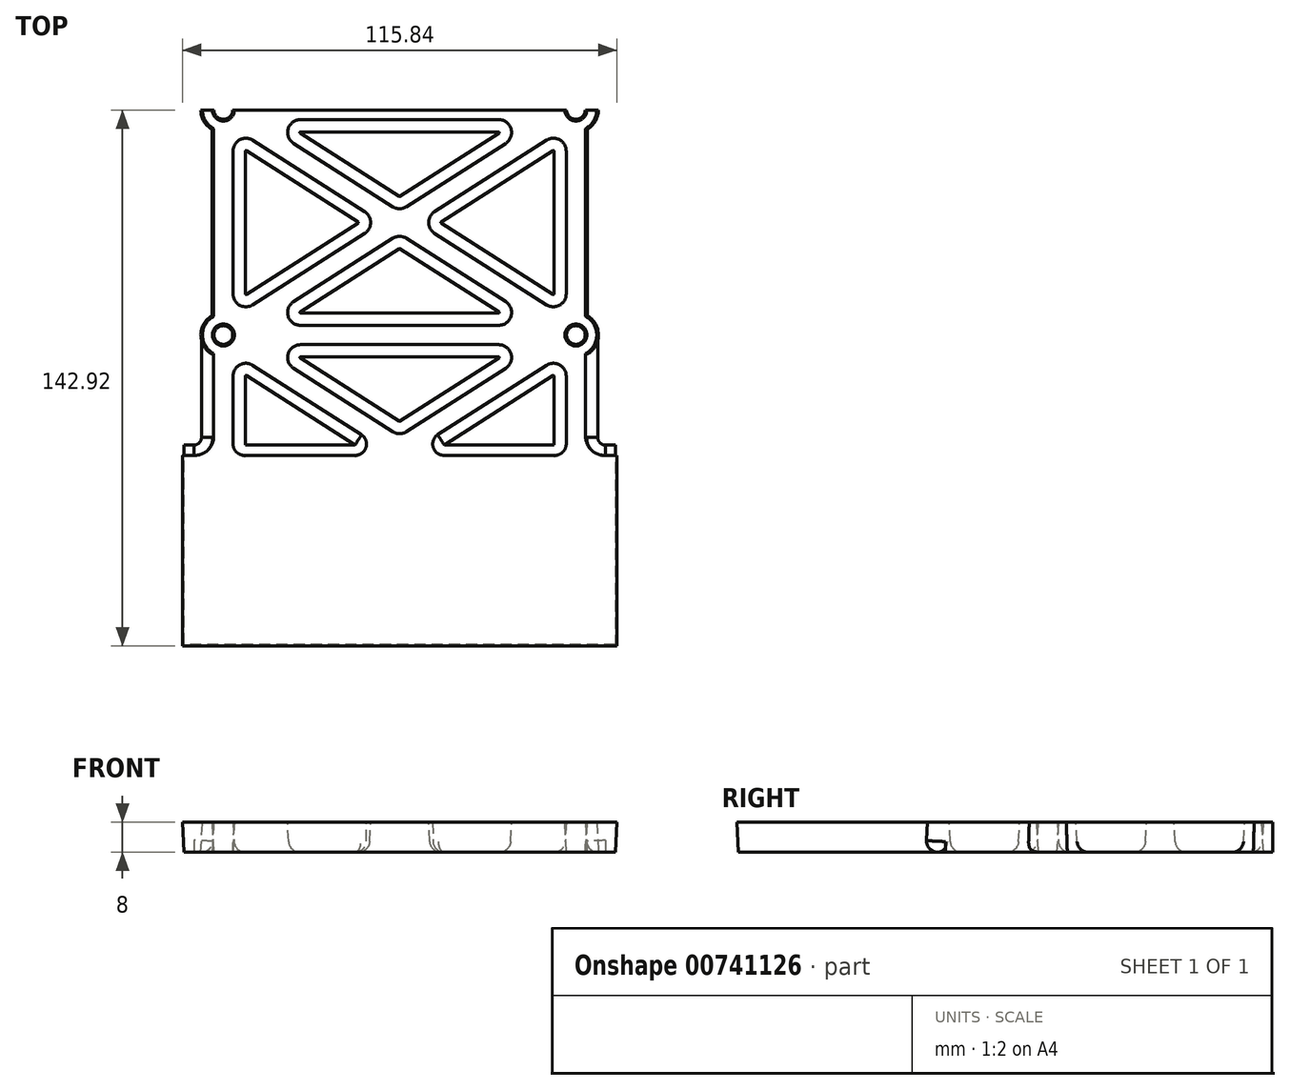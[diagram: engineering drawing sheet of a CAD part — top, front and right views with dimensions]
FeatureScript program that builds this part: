
annotation { "Feature Type Name" : "Feature", "Feature Type Description" : "" }
export const myFeature = defineFeature(function(context is Context, id is Id, definition is map)
    precondition{}
    {
        {
            var Q0;
            Q0=qCreatedBy(makeId("Top.planeOp"),FACE);
            var sketch = newSketch(context, id + "F0", { "sketchPlane" : qUnion([Q0])});
            skArc(sketch, "E0", {"start": v(49.5, 0) * mm, "mid": v(47, 2.5) * mm, "end": v(44.5, 0) * mm});
            skArc(sketch, "E1", {"start": v(53, 0) * mm, "mid": v(52.2, 3) * mm, "end": v(50, 5.2) * mm});
            skArc(sketch, "E2.0.1.0", {"start": v(50, 54.8) * mm, "mid": v(53, 60) * mm, "end": v(50, 65.2) * mm});
            skCircle(sketch, "E2.0.1.1", {"center": v(47, 60) * mm, "radius": 2.5 * mm});
            skArc(sketch, "E2.0.2.0", {"start": v(50, 114.8) * mm, "mid": v(51.24, 124.24) * mm, "end": v(41.8, 123) * mm});
            skCircle(sketch, "E2.0.2.1", {"center": v(47, 120) * mm, "radius": 2.5 * mm});
            skArc(sketch, "E2.1.0.0", {"start": v(-50, 5.2) * mm, "mid": v(-52.2, 3) * mm, "end": v(-53, 0) * mm});
            skArc(sketch, "E2.1.0.1", {"start": v(-44.5, 0) * mm, "mid": v(-47, 2.5) * mm, "end": v(-49.5, 0) * mm});
            skArc(sketch, "E2.1.1.0", {"start": v(-50, 65.2) * mm, "mid": v(-53, 60) * mm, "end": v(-50, 54.8) * mm});
            skCircle(sketch, "E2.1.1.1", {"center": v(-47, 60) * mm, "radius": 2.5 * mm});
            skArc(sketch, "E2.1.2.0", {"start": v(-41.8, 123) * mm, "mid": v(-51.24, 124.24) * mm, "end": v(-50, 114.8) * mm});
            skCircle(sketch, "E2.1.2.1", {"center": v(-47, 120) * mm, "radius": 2.5 * mm});
            skLineSegment(sketch, "E2.direction1", {"start": v(44.5, 0) * mm, "end": v(-44.5, 0) * mm, "construction": true});
            skLineSegment(sketch, "E3.0", {"start": v(-44, 109.05) * mm, "end": v(-44, 70.95) * mm});
            skLineSegment(sketch, "E3.1", {"start": v(-9.54, 92.53) * mm, "end": v(-39.39, 111.58) * mm});
            skLineSegment(sketch, "E3.2", {"start": v(-9.54, 87.47) * mm, "end": v(-39.39, 68.42) * mm});
            skArc(sketch, "E4.filletArc", {"start": v(-9.54, 87.47) * mm, "mid": v(-8.15, 90) * mm, "end": v(-9.54, 92.53) * mm});
            skArc(sketch, "E5.filletArc", {"start": v(-44, 70.95) * mm, "mid": v(-42.44, 68.32) * mm, "end": v(-39.39, 68.42) * mm});
            skArc(sketch, "E6.filletArc", {"start": v(-39.39, 111.58) * mm, "mid": v(-42.44, 111.68) * mm, "end": v(-44, 109.05) * mm});
            skLineSegment(sketch, "E7.0", {"start": v(26.45, 117) * mm, "end": v(-26.45, 117) * mm});
            skLineSegment(sketch, "E7.1", {"start": v(28.06, 111.47) * mm, "end": v(1.61, 94.59) * mm});
            skLineSegment(sketch, "E7.2", {"start": v(-1.61, 94.59) * mm, "end": v(-28.06, 111.47) * mm});
            skArc(sketch, "E8.filletArc", {"start": v(-26.45, 117) * mm, "mid": v(-29.33, 114.84) * mm, "end": v(-28.06, 111.47) * mm});
            skArc(sketch, "E9.filletArc", {"start": v(28.06, 111.47) * mm, "mid": v(29.33, 114.84) * mm, "end": v(26.45, 117) * mm});
            skArc(sketch, "E10.filletArc", {"start": v(-1.61, 94.59) * mm, "mid": v(0, 94.12) * mm, "end": v(1.61, 94.59) * mm});
            skLineSegment(sketch, "E11.0", {"start": v(-50, 114.8) * mm, "end": v(-50, 65.2) * mm});
            skLineSegment(sketch, "E12.0", {"start": v(41.8, 123) * mm, "end": v(-41.8, 123) * mm});
            skLineSegment(sketch, "E13.MirrorCS", {"start": v(44, 109.05) * mm, "end": v(44, 70.95) * mm});
            skArc(sketch, "E14.MirrorCS", {"start": v(39.39, 111.58) * mm, "mid": v(42.44, 111.68) * mm, "end": v(44, 109.05) * mm});
            skLineSegment(sketch, "E15.MirrorCS", {"start": v(9.54, 92.53) * mm, "end": v(39.39, 111.58) * mm});
            skArc(sketch, "E16.MirrorCS", {"start": v(9.54, 87.47) * mm, "mid": v(8.15, 90) * mm, "end": v(9.54, 92.53) * mm});
            skLineSegment(sketch, "E17.MirrorCS", {"start": v(9.54, 87.47) * mm, "end": v(39.39, 68.42) * mm});
            skArc(sketch, "E18.MirrorCS", {"start": v(44, 70.95) * mm, "mid": v(42.44, 68.32) * mm, "end": v(39.39, 68.42) * mm});
            skLineSegment(sketch, "E19.MirrorCS", {"start": v(26.45, 63) * mm, "end": v(-26.45, 63) * mm});
            skArc(sketch, "E20.MirrorCS", {"start": v(28.06, 68.53) * mm, "mid": v(29.33, 65.16) * mm, "end": v(26.45, 63) * mm});
            skLineSegment(sketch, "E21.MirrorCS", {"start": v(28.06, 68.53) * mm, "end": v(1.61, 85.41) * mm});
            skLineSegment(sketch, "E22.MirrorCS", {"start": v(-1.61, 85.41) * mm, "end": v(-28.06, 68.53) * mm});
            skArc(sketch, "E23.MirrorCS", {"start": v(-26.45, 63) * mm, "mid": v(-29.33, 65.16) * mm, "end": v(-28.06, 68.53) * mm});
            skArc(sketch, "E24.MirrorCS", {"start": v(-1.61, 85.41) * mm, "mid": v(0, 85.88) * mm, "end": v(1.61, 85.41) * mm});
            skLineSegment(sketch, "E25.0", {"start": v(50, 114.8) * mm, "end": v(50, 65.2) * mm});
            skArc(sketch, "E26.MirrorCS", {"start": v(-1.61, 34.59) * mm, "mid": v(0, 34.12) * mm, "end": v(1.61, 34.59) * mm});
            skArc(sketch, "E27.MirrorCS", {"start": v(-1.61, 25.41) * mm, "mid": v(0, 25.88) * mm, "end": v(1.61, 25.41) * mm});
            skArc(sketch, "E28.MirrorCS", {"start": v(39.39, 8.42) * mm, "mid": v(42.44, 8.32) * mm, "end": v(44, 10.95) * mm});
            skArc(sketch, "E29.MirrorCS", {"start": v(-26.45, 57) * mm, "mid": v(-29.33, 54.84) * mm, "end": v(-28.06, 51.47) * mm});
            skArc(sketch, "E30.MirrorCS", {"start": v(44, 49.05) * mm, "mid": v(42.44, 51.68) * mm, "end": v(39.39, 51.58) * mm});
            skArc(sketch, "E31.MirrorCS", {"start": v(9.54, 32.53) * mm, "mid": v(8.15, 30) * mm, "end": v(9.54, 27.47) * mm});
            skArc(sketch, "E32.MirrorCS", {"start": v(28.06, 51.47) * mm, "mid": v(29.33, 54.84) * mm, "end": v(26.45, 57) * mm});
            skArc(sketch, "E33.MirrorCS", {"start": v(-39.39, 8.42) * mm, "mid": v(-42.44, 8.32) * mm, "end": v(-44, 10.95) * mm});
            skArc(sketch, "E34.MirrorCS", {"start": v(-44, 49.05) * mm, "mid": v(-42.44, 51.68) * mm, "end": v(-39.39, 51.58) * mm});
            skArc(sketch, "E35.MirrorCS", {"start": v(-9.54, 32.53) * mm, "mid": v(-8.15, 30) * mm, "end": v(-9.54, 27.47) * mm});
            skArc(sketch, "E36.MirrorCS", {"start": v(28.06, 8.53) * mm, "mid": v(29.33, 5.16) * mm, "end": v(26.45, 3) * mm});
            skArc(sketch, "E37.MirrorCS", {"start": v(-26.45, 3) * mm, "mid": v(-29.33, 5.16) * mm, "end": v(-28.06, 8.53) * mm});
            skLineSegment(sketch, "E38.MirrorCS", {"start": v(26.45, 57) * mm, "end": v(-26.45, 57) * mm});
            skLineSegment(sketch, "E39.MirrorCS", {"start": v(28.06, 51.47) * mm, "end": v(1.61, 34.59) * mm});
            skLineSegment(sketch, "E40.MirrorCS", {"start": v(-44, 10.95) * mm, "end": v(-44, 49.05) * mm});
            skLineSegment(sketch, "E41.MirrorCS", {"start": v(44, 10.95) * mm, "end": v(44, 49.05) * mm});
            skLineSegment(sketch, "E42.MirrorCS", {"start": v(9.54, 27.47) * mm, "end": v(39.39, 8.42) * mm});
            skLineSegment(sketch, "E43.MirrorCS", {"start": v(-9.54, 27.47) * mm, "end": v(-39.39, 8.42) * mm});
            skLineSegment(sketch, "E44.MirrorCS", {"start": v(28.06, 8.53) * mm, "end": v(1.61, 25.41) * mm});
            skLineSegment(sketch, "E45.MirrorCS", {"start": v(-9.54, 32.53) * mm, "end": v(-39.39, 51.58) * mm});
            skLineSegment(sketch, "E46.MirrorCS", {"start": v(-1.61, 34.59) * mm, "end": v(-28.06, 51.47) * mm});
            skLineSegment(sketch, "E47.MirrorCS", {"start": v(9.54, 32.53) * mm, "end": v(39.39, 51.58) * mm});
            skLineSegment(sketch, "E48.MirrorCS", {"start": v(-1.61, 25.41) * mm, "end": v(-28.06, 8.53) * mm});
            skLineSegment(sketch, "E49.MirrorCS", {"start": v(26.45, 3) * mm, "end": v(-26.45, 3) * mm});
            skLineSegment(sketch, "E50.0", {"start": v(-50, 54.8) * mm, "end": v(-50, 5.2) * mm});
            skLineSegment(sketch, "E51.0", {"start": v(50, 54.8) * mm, "end": v(50, 5.2) * mm});
            skLineSegment(sketch, "E52", {"start": v(-53, 0) * mm, "end": v(-49.5, 0) * mm});
            skLineSegment(sketch, "E53.trimOffspring", {"start": v(-44.5, 0) * mm, "end": v(44.5, 0) * mm});
            skLineSegment(sketch, "E54.trimOffspring", {"start": v(49.5, 0) * mm, "end": v(53, 0) * mm});
            skArc(sketch, "E55.MirrorCS", {"start": v(-44.5, 0) * mm, "mid": v(-47, -2.5) * mm, "end": v(-49.5, 0) * mm});
            skArc(sketch, "E56.MirrorCS", {"start": v(-1.61, -25.41) * mm, "mid": v(0, -25.88) * mm, "end": v(1.61, -25.41) * mm});
            skArc(sketch, "E57.MirrorCS", {"start": v(-9.54, -32.53) * mm, "mid": v(-8.15, -30) * mm, "end": v(-9.54, -27.47) * mm});
            skCircle(sketch, "E58.MirrorC", {"center": v(47, -120) * mm, "radius": 2.5 * mm});
            skArc(sketch, "E59.MirrorCS", {"start": v(-50, -5.2) * mm, "mid": v(-52.2, -3) * mm, "end": v(-53, 0) * mm});
            skArc(sketch, "E60.MirrorCS", {"start": v(-39.39, -8.42) * mm, "mid": v(-42.44, -8.32) * mm, "end": v(-44, -10.95) * mm});
            skArc(sketch, "E61.MirrorCS", {"start": v(-1.61, -85.41) * mm, "mid": v(0, -85.88) * mm, "end": v(1.61, -85.41) * mm});
            skArc(sketch, "E62.MirrorCS", {"start": v(39.39, -8.42) * mm, "mid": v(42.44, -8.32) * mm, "end": v(44, -10.95) * mm});
            skArc(sketch, "E63.MirrorCS", {"start": v(28.06, -68.53) * mm, "mid": v(29.33, -65.16) * mm, "end": v(26.45, -63) * mm});
            skArc(sketch, "E64.MirrorCS", {"start": v(-39.39, -111.58) * mm, "mid": v(-42.44, -111.68) * mm, "end": v(-44, -109.05) * mm});
            skArc(sketch, "E65.MirrorCS", {"start": v(28.06, -111.47) * mm, "mid": v(29.33, -114.84) * mm, "end": v(26.45, -117) * mm});
            skArc(sketch, "E66.MirrorCS", {"start": v(49.5, 0) * mm, "mid": v(47, -2.5) * mm, "end": v(44.5, 0) * mm});
            skArc(sketch, "E67.MirrorCS", {"start": v(44, -70.95) * mm, "mid": v(42.44, -68.32) * mm, "end": v(39.39, -68.42) * mm});
            skArc(sketch, "E68.MirrorCS", {"start": v(-26.45, -3) * mm, "mid": v(-29.33, -5.16) * mm, "end": v(-28.06, -8.53) * mm});
            skArc(sketch, "E69.MirrorCS", {"start": v(39.39, -111.58) * mm, "mid": v(42.44, -111.68) * mm, "end": v(44, -109.05) * mm});
            skArc(sketch, "E70.MirrorCS", {"start": v(-1.61, -94.59) * mm, "mid": v(0, -94.12) * mm, "end": v(1.61, -94.59) * mm});
            skArc(sketch, "E71.MirrorCS", {"start": v(-26.45, -63) * mm, "mid": v(-29.33, -65.16) * mm, "end": v(-28.06, -68.53) * mm});
            skArc(sketch, "E72.MirrorCS", {"start": v(44, -49.05) * mm, "mid": v(42.44, -51.68) * mm, "end": v(39.39, -51.58) * mm});
            skArc(sketch, "E73.MirrorCS", {"start": v(28.06, -8.53) * mm, "mid": v(29.33, -5.16) * mm, "end": v(26.45, -3) * mm});
            skArc(sketch, "E74.MirrorCS", {"start": v(-44, -70.95) * mm, "mid": v(-42.44, -68.32) * mm, "end": v(-39.39, -68.42) * mm});
            skArc(sketch, "E75.MirrorCS", {"start": v(-44, -49.05) * mm, "mid": v(-42.44, -51.68) * mm, "end": v(-39.39, -51.58) * mm});
            skArc(sketch, "E76.MirrorCS", {"start": v(9.54, -32.53) * mm, "mid": v(8.15, -30) * mm, "end": v(9.54, -27.47) * mm});
            skArc(sketch, "E77.MirrorCS", {"start": v(-26.45, -57) * mm, "mid": v(-29.33, -54.84) * mm, "end": v(-28.06, -51.47) * mm});
            skArc(sketch, "E78.MirrorCS", {"start": v(-26.45, -117) * mm, "mid": v(-29.33, -114.84) * mm, "end": v(-28.06, -111.47) * mm});
            skArc(sketch, "E79.MirrorCS", {"start": v(-9.54, -87.47) * mm, "mid": v(-8.15, -90) * mm, "end": v(-9.54, -92.53) * mm});
            skArc(sketch, "E80.MirrorCS", {"start": v(28.06, -51.47) * mm, "mid": v(29.33, -54.84) * mm, "end": v(26.45, -57) * mm});
            skArc(sketch, "E81.MirrorCS", {"start": v(53, 0) * mm, "mid": v(52.2, -3) * mm, "end": v(50, -5.2) * mm});
            skArc(sketch, "E82.MirrorCS", {"start": v(9.54, -87.47) * mm, "mid": v(8.15, -90) * mm, "end": v(9.54, -92.53) * mm});
            skArc(sketch, "E83.MirrorCS", {"start": v(-1.61, -34.59) * mm, "mid": v(0, -34.12) * mm, "end": v(1.61, -34.59) * mm});
            skCircle(sketch, "E84.MirrorC", {"center": v(-47, -60) * mm, "radius": 2.5 * mm});
            skCircle(sketch, "E85.MirrorC", {"center": v(-47, -120) * mm, "radius": 2.5 * mm});
            skLineSegment(sketch, "E86.MirrorCS", {"start": v(26.45, -57) * mm, "end": v(-26.45, -57) * mm});
            skLineSegment(sketch, "E87.MirrorCS", {"start": v(9.54, -87.47) * mm, "end": v(39.39, -68.42) * mm});
            skLineSegment(sketch, "E88.MirrorCS", {"start": v(28.06, -111.47) * mm, "end": v(1.61, -94.59) * mm});
            skLineSegment(sketch, "E89.MirrorCS", {"start": v(-1.61, -34.59) * mm, "end": v(-28.06, -51.47) * mm});
            skLineSegment(sketch, "E90.MirrorCS", {"start": v(-9.54, -87.47) * mm, "end": v(-39.39, -68.42) * mm});
            skArc(sketch, "E91.MirrorCS", {"start": v(-50, -65.2) * mm, "mid": v(-53, -60) * mm, "end": v(-50, -54.8) * mm});
            skLineSegment(sketch, "E92.MirrorCS", {"start": v(-1.61, -94.59) * mm, "end": v(-28.06, -111.47) * mm});
            skLineSegment(sketch, "E93.MirrorCS", {"start": v(28.06, -51.47) * mm, "end": v(1.61, -34.59) * mm});
            skLineSegment(sketch, "E94.MirrorCS", {"start": v(28.06, -8.53) * mm, "end": v(1.61, -25.41) * mm});
            skLineSegment(sketch, "E95.MirrorCS", {"start": v(26.45, -117) * mm, "end": v(-26.45, -117) * mm});
            skLineSegment(sketch, "E96.MirrorCS", {"start": v(44, -109.05) * mm, "end": v(44, -70.95) * mm});
            skArc(sketch, "E97.MirrorCS", {"start": v(50, -54.8) * mm, "mid": v(53, -60) * mm, "end": v(50, -65.2) * mm});
            skLineSegment(sketch, "E98.MirrorCS", {"start": v(-9.54, -27.47) * mm, "end": v(-39.39, -8.42) * mm});
            skLineSegment(sketch, "E99.MirrorCS", {"start": v(44, -10.95) * mm, "end": v(44, -49.05) * mm});
            skLineSegment(sketch, "E100.MirrorCS", {"start": v(26.45, -63) * mm, "end": v(-26.45, -63) * mm});
            skLineSegment(sketch, "E101.MirrorCS", {"start": v(-44, -109.05) * mm, "end": v(-44, -70.95) * mm});
            skCircle(sketch, "E102.MirrorC", {"center": v(47, -60) * mm, "radius": 2.5 * mm});
            skLineSegment(sketch, "E103.MirrorCS", {"start": v(-9.54, -32.53) * mm, "end": v(-39.39, -51.58) * mm});
            skArc(sketch, "E104.MirrorCS", {"start": v(50, -114.8) * mm, "mid": v(51.24, -124.24) * mm, "end": v(41.8, -123) * mm});
            skLineSegment(sketch, "E105.MirrorCS", {"start": v(9.54, -27.47) * mm, "end": v(39.39, -8.42) * mm});
            skLineSegment(sketch, "E106.MirrorCS", {"start": v(9.54, -92.53) * mm, "end": v(39.39, -111.58) * mm});
            skLineSegment(sketch, "E107.MirrorCS", {"start": v(50, -114.8) * mm, "end": v(50, -65.2) * mm});
            skLineSegment(sketch, "E108.MirrorCS", {"start": v(-44, -10.95) * mm, "end": v(-44, -49.05) * mm});
            skLineSegment(sketch, "E109.MirrorCS", {"start": v(-1.61, -85.41) * mm, "end": v(-28.06, -68.53) * mm});
            skLineSegment(sketch, "E110.MirrorCS", {"start": v(41.8, -123) * mm, "end": v(-41.8, -123) * mm});
            skLineSegment(sketch, "E111.MirrorCS", {"start": v(26.45, -3) * mm, "end": v(-26.45, -3) * mm});
            skLineSegment(sketch, "E112.MirrorCS", {"start": v(9.54, -32.53) * mm, "end": v(39.39, -51.58) * mm});
            skLineSegment(sketch, "E113.MirrorCS", {"start": v(50, -54.8) * mm, "end": v(50, -5.2) * mm});
            skLineSegment(sketch, "E114.MirrorCS", {"start": v(-50, -114.8) * mm, "end": v(-50, -65.2) * mm});
            skLineSegment(sketch, "E115.MirrorCS", {"start": v(28.06, -68.53) * mm, "end": v(1.61, -85.41) * mm});
            skArc(sketch, "E116.MirrorCS", {"start": v(-41.8, -123) * mm, "mid": v(-51.24, -124.24) * mm, "end": v(-50, -114.8) * mm});
            skLineSegment(sketch, "E117.MirrorCS", {"start": v(-1.61, -25.41) * mm, "end": v(-28.06, -8.53) * mm});
            skLineSegment(sketch, "E118.MirrorCS", {"start": v(-9.54, -92.53) * mm, "end": v(-39.39, -111.58) * mm});
            skLineSegment(sketch, "E119.MirrorCS", {"start": v(-50, -54.8) * mm, "end": v(-50, -5.2) * mm});
            skSolve(sketch);
        }
        {
            var Q0;
            Q0=qSketchRegion(id+"F0",true);
            extrude(context, id + "F1", {"entities" : qUnion([Q0]), "depth" : 8 * mm, "offsetDistance" : 25 * mm, "hasDraft" : true, "draftAngle" : 3 * degree, "draftPullDirection" : true});
        }
        {
            var Q0;
            Q0=qCreatedBy(makeId("Top.planeOp"),FACE);
            var sketch = newSketch(context, id + "F2", { "sketchPlane" : qUnion([Q0])});
            skLineSegment(sketch, "E120.bottom", {"start": v(57.5, 142.5) * mm, "end": v(-57.5, 142.5) * mm});
            skLineSegment(sketch, "E120.top", {"start": v(57.5, -142.5) * mm, "end": v(-57.5, -142.5) * mm});
            skLineSegment(sketch, "E120.left", {"start": v(57.5, 142.5) * mm, "end": v(57.5, -142.5) * mm});
            skLineSegment(sketch, "E120.right", {"start": v(-57.5, 142.5) * mm, "end": v(-57.5, -142.5) * mm});
            skSolve(sketch);
        }
        {
            var Q0;
            Q0=qSketchRegion(id+"F2",true);
            extrude(context, id + "F3", {"entities" : qUnion([Q0]), "operationType" : NewBodyOperationType.ADD, "depth" : -2 * mm, "offsetDistance" : 25 * mm});
        }
        {
            var Q0;
            Q0=makeQuery(id+"F3.boolean.opBoolean","SPLIT",FACE,{"disambiguationData":[TD([makeQuery(id+"F1.opExtrude","SWEPT_FACE",FACE,{"disambiguationData":[OSD([sQuery(id+"F0.wireOp",EDGE,"E7.0")])]})])],"derivedFrom":makeQuery(id+"F3.opExtrude","CAP_FACE",FACE,{"disambiguationData":[OSD([sQuery(id+"F2.wireOp",EDGE,"E120.bottom"),sQuery(id+"F2.wireOp",EDGE,"E120.top"),sQuery(id+"F2.wireOp",EDGE,"E120.left"),sQuery(id+"F2.wireOp",EDGE,"E120.right")])],"isStart":true})});
            var Q1;
            Q1=makeQuery(id+"F3.boolean.opBoolean","SPLIT",FACE,{"disambiguationData":[TD([makeQuery(id+"F1.opExtrude","SWEPT_FACE",FACE,{"disambiguationData":[OSD([sQuery(id+"F0.wireOp",EDGE,"E3.0")])]})])],"derivedFrom":makeQuery(id+"F3.opExtrude","CAP_FACE",FACE,{"disambiguationData":[OSD([sQuery(id+"F2.wireOp",EDGE,"E120.bottom"),sQuery(id+"F2.wireOp",EDGE,"E120.top"),sQuery(id+"F2.wireOp",EDGE,"E120.left"),sQuery(id+"F2.wireOp",EDGE,"E120.right")])],"isStart":true})});
            var Q2;
            Q2=makeQuery(id+"F3.boolean.opBoolean","SPLIT",FACE,{"disambiguationData":[TD([makeQuery(id+"F1.opExtrude","SWEPT_FACE",FACE,{"disambiguationData":[OSD([sQuery(id+"F0.wireOp",EDGE,"E13.MirrorCS")])]})])],"derivedFrom":makeQuery(id+"F3.opExtrude","CAP_FACE",FACE,{"disambiguationData":[OSD([sQuery(id+"F2.wireOp",EDGE,"E120.bottom"),sQuery(id+"F2.wireOp",EDGE,"E120.top"),sQuery(id+"F2.wireOp",EDGE,"E120.left"),sQuery(id+"F2.wireOp",EDGE,"E120.right")])],"isStart":true})});
            var Q3;
            Q3=makeQuery(id+"F3.boolean.opBoolean","SPLIT",FACE,{"disambiguationData":[TD([makeQuery(id+"F1.opExtrude","SWEPT_FACE",FACE,{"disambiguationData":[OSD([sQuery(id+"F0.wireOp",EDGE,"E19.MirrorCS")])]})])],"derivedFrom":makeQuery(id+"F3.opExtrude","CAP_FACE",FACE,{"disambiguationData":[OSD([sQuery(id+"F2.wireOp",EDGE,"E120.bottom"),sQuery(id+"F2.wireOp",EDGE,"E120.top"),sQuery(id+"F2.wireOp",EDGE,"E120.left"),sQuery(id+"F2.wireOp",EDGE,"E120.right")])],"isStart":true})});
            var Q4;
            Q4=makeQuery(id+"F3.boolean.opBoolean","SPLIT",FACE,{"disambiguationData":[TD([makeQuery(id+"F1.opExtrude","SWEPT_FACE",FACE,{"disambiguationData":[OSD([sQuery(id+"F0.wireOp",EDGE,"E33.MirrorCS")])]})])],"derivedFrom":makeQuery(id+"F3.opExtrude","CAP_FACE",FACE,{"disambiguationData":[OSD([sQuery(id+"F2.wireOp",EDGE,"E120.bottom"),sQuery(id+"F2.wireOp",EDGE,"E120.top"),sQuery(id+"F2.wireOp",EDGE,"E120.left"),sQuery(id+"F2.wireOp",EDGE,"E120.right")])],"isStart":true})});
            var Q5;
            Q5=makeQuery(id+"F3.boolean.opBoolean","SPLIT",FACE,{"disambiguationData":[TD([makeQuery(id+"F1.opExtrude","SWEPT_FACE",FACE,{"disambiguationData":[OSD([sQuery(id+"F0.wireOp",EDGE,"E26.MirrorCS")])]})])],"derivedFrom":makeQuery(id+"F3.opExtrude","CAP_FACE",FACE,{"disambiguationData":[OSD([sQuery(id+"F2.wireOp",EDGE,"E120.bottom"),sQuery(id+"F2.wireOp",EDGE,"E120.top"),sQuery(id+"F2.wireOp",EDGE,"E120.left"),sQuery(id+"F2.wireOp",EDGE,"E120.right")])],"isStart":true})});
            var Q6;
            Q6=makeQuery(id+"F3.boolean.opBoolean","SPLIT",FACE,{"disambiguationData":[TD([makeQuery(id+"F1.opExtrude","SWEPT_FACE",FACE,{"disambiguationData":[OSD([sQuery(id+"F0.wireOp",EDGE,"E28.MirrorCS")])]})])],"derivedFrom":makeQuery(id+"F3.opExtrude","CAP_FACE",FACE,{"disambiguationData":[OSD([sQuery(id+"F2.wireOp",EDGE,"E120.bottom"),sQuery(id+"F2.wireOp",EDGE,"E120.top"),sQuery(id+"F2.wireOp",EDGE,"E120.left"),sQuery(id+"F2.wireOp",EDGE,"E120.right")])],"isStart":true})});
            var Q7;
            Q7=makeQuery(id+"F3.boolean.opBoolean","SPLIT",FACE,{"disambiguationData":[TD([makeQuery(id+"F1.opExtrude","SWEPT_FACE",FACE,{"disambiguationData":[OSD([sQuery(id+"F0.wireOp",EDGE,"E27.MirrorCS")])]})])],"derivedFrom":makeQuery(id+"F3.opExtrude","CAP_FACE",FACE,{"disambiguationData":[OSD([sQuery(id+"F2.wireOp",EDGE,"E120.bottom"),sQuery(id+"F2.wireOp",EDGE,"E120.top"),sQuery(id+"F2.wireOp",EDGE,"E120.left"),sQuery(id+"F2.wireOp",EDGE,"E120.right")])],"isStart":true})});
            var Q8;
            Q8=makeQuery(id+"F3.boolean.opBoolean","SPLIT",FACE,{"disambiguationData":[TD([makeQuery(id+"F1.opExtrude","SWEPT_FACE",FACE,{"disambiguationData":[OSD([sQuery(id+"F0.wireOp",EDGE,"E56.MirrorCS")])]})])],"derivedFrom":makeQuery(id+"F3.opExtrude","CAP_FACE",FACE,{"disambiguationData":[OSD([sQuery(id+"F2.wireOp",EDGE,"E120.bottom"),sQuery(id+"F2.wireOp",EDGE,"E120.top"),sQuery(id+"F2.wireOp",EDGE,"E120.left"),sQuery(id+"F2.wireOp",EDGE,"E120.right")])],"isStart":true})});
            var Q9;
            Q9=makeQuery(id+"F3.boolean.opBoolean","SPLIT",FACE,{"disambiguationData":[TD([makeQuery(id+"F1.opExtrude","SWEPT_FACE",FACE,{"disambiguationData":[OSD([sQuery(id+"F0.wireOp",EDGE,"E62.MirrorCS")])]})])],"derivedFrom":makeQuery(id+"F3.opExtrude","CAP_FACE",FACE,{"disambiguationData":[OSD([sQuery(id+"F2.wireOp",EDGE,"E120.bottom"),sQuery(id+"F2.wireOp",EDGE,"E120.top"),sQuery(id+"F2.wireOp",EDGE,"E120.left"),sQuery(id+"F2.wireOp",EDGE,"E120.right")])],"isStart":true})});
            var Q10;
            Q10=makeQuery(id+"F3.boolean.opBoolean","SPLIT",FACE,{"disambiguationData":[TD([makeQuery(id+"F1.opExtrude","SWEPT_FACE",FACE,{"disambiguationData":[OSD([sQuery(id+"F0.wireOp",EDGE,"E57.MirrorCS")])]})])],"derivedFrom":makeQuery(id+"F3.opExtrude","CAP_FACE",FACE,{"disambiguationData":[OSD([sQuery(id+"F2.wireOp",EDGE,"E120.bottom"),sQuery(id+"F2.wireOp",EDGE,"E120.top"),sQuery(id+"F2.wireOp",EDGE,"E120.left"),sQuery(id+"F2.wireOp",EDGE,"E120.right")])],"isStart":true})});
            var Q11;
            Q11=makeQuery(id+"F3.boolean.opBoolean","SPLIT",FACE,{"disambiguationData":[TD([makeQuery(id+"F1.opExtrude","SWEPT_FACE",FACE,{"disambiguationData":[OSD([sQuery(id+"F0.wireOp",EDGE,"E77.MirrorCS")])]})])],"derivedFrom":makeQuery(id+"F3.opExtrude","CAP_FACE",FACE,{"disambiguationData":[OSD([sQuery(id+"F2.wireOp",EDGE,"E120.bottom"),sQuery(id+"F2.wireOp",EDGE,"E120.top"),sQuery(id+"F2.wireOp",EDGE,"E120.left"),sQuery(id+"F2.wireOp",EDGE,"E120.right")])],"isStart":true})});
            var Q12;
            Q12=makeQuery(id+"F3.boolean.opBoolean","SPLIT",FACE,{"disambiguationData":[TD([makeQuery(id+"F1.opExtrude","SWEPT_FACE",FACE,{"disambiguationData":[OSD([sQuery(id+"F0.wireOp",EDGE,"E61.MirrorCS")])]})])],"derivedFrom":makeQuery(id+"F3.opExtrude","CAP_FACE",FACE,{"disambiguationData":[OSD([sQuery(id+"F2.wireOp",EDGE,"E120.bottom"),sQuery(id+"F2.wireOp",EDGE,"E120.top"),sQuery(id+"F2.wireOp",EDGE,"E120.left"),sQuery(id+"F2.wireOp",EDGE,"E120.right")])],"isStart":true})});
            var Q13;
            Q13=makeQuery(id+"F3.boolean.opBoolean","SPLIT",FACE,{"disambiguationData":[TD([makeQuery(id+"F1.opExtrude","SWEPT_FACE",FACE,{"disambiguationData":[OSD([sQuery(id+"F0.wireOp",EDGE,"E64.MirrorCS")])]})])],"derivedFrom":makeQuery(id+"F3.opExtrude","CAP_FACE",FACE,{"disambiguationData":[OSD([sQuery(id+"F2.wireOp",EDGE,"E120.bottom"),sQuery(id+"F2.wireOp",EDGE,"E120.top"),sQuery(id+"F2.wireOp",EDGE,"E120.left"),sQuery(id+"F2.wireOp",EDGE,"E120.right")])],"isStart":true})});
            var Q14;
            Q14=makeQuery(id+"F3.boolean.opBoolean","SPLIT",FACE,{"disambiguationData":[TD([makeQuery(id+"F1.opExtrude","SWEPT_FACE",FACE,{"disambiguationData":[OSD([sQuery(id+"F0.wireOp",EDGE,"E65.MirrorCS")])]})])],"derivedFrom":makeQuery(id+"F3.opExtrude","CAP_FACE",FACE,{"disambiguationData":[OSD([sQuery(id+"F2.wireOp",EDGE,"E120.bottom"),sQuery(id+"F2.wireOp",EDGE,"E120.top"),sQuery(id+"F2.wireOp",EDGE,"E120.left"),sQuery(id+"F2.wireOp",EDGE,"E120.right")])],"isStart":true})});
            var Q15;
            Q15=makeQuery(id+"F3.boolean.opBoolean","SPLIT",FACE,{"disambiguationData":[TD([makeQuery(id+"F1.opExtrude","SWEPT_FACE",FACE,{"disambiguationData":[OSD([sQuery(id+"F0.wireOp",EDGE,"E67.MirrorCS")])]})])],"derivedFrom":makeQuery(id+"F3.opExtrude","CAP_FACE",FACE,{"disambiguationData":[OSD([sQuery(id+"F2.wireOp",EDGE,"E120.bottom"),sQuery(id+"F2.wireOp",EDGE,"E120.top"),sQuery(id+"F2.wireOp",EDGE,"E120.left"),sQuery(id+"F2.wireOp",EDGE,"E120.right")])],"isStart":true})});
            fillet(context, id + "F4", {"entities" : qUnion([Q0, Q1, Q2, Q3, Q4, Q5, Q6, Q7, Q8, Q9, Q10, Q11, Q12, Q13, Q14, Q15]), "radius" : 3 * mm, "tangentPropagation" : true, "allowEdgeOverflow" : false});
        }
        {
            var Q0;
            Q0=qCreatedBy(makeId("Top.planeOp"),FACE);
            var sketch = newSketch(context, id + "F5", { "sketchPlane" : qUnion([Q0])});
            skLineSegment(sketch, "E121.bottom", {"start": v(-57.5, -142.5) * mm, "end": v(57.5, -142.5) * mm});
            skLineSegment(sketch, "E121.top", {"start": v(-57.5, -92.5) * mm, "end": v(57.5, -92.5) * mm});
            skLineSegment(sketch, "E121.left", {"start": v(-57.5, -142.5) * mm, "end": v(-57.5, -92.5) * mm});
            skLineSegment(sketch, "E121.right", {"start": v(57.5, -142.5) * mm, "end": v(57.5, -92.5) * mm});
            skSolve(sketch);
        }
        {
            var Q0;
            Q0=qSketchRegion(id+"F5",true);
            extrude(context, id + "F6", {"entities" : qUnion([Q0]), "operationType" : NewBodyOperationType.ADD, "depth" : 8 * mm, "offsetDistance" : 25 * mm, "hasDraft" : true, "draftAngle" : 3 * degree});
        }
        {
            var Q0;
            Q0=makeQuery(id+"F3.boolean.opBoolean","SPLIT",FACE,{"disambiguationData":[TD([makeQuery(id+"F1.opExtrude","SWEPT_FACE",FACE,{"disambiguationData":[OSD([sQuery(id+"F0.wireOp",EDGE,"E64.MirrorCS")])]})])],"derivedFrom":makeQuery(id+"F3.opExtrude","CAP_FACE",FACE,{"disambiguationData":[OSD([sQuery(id+"F2.wireOp",EDGE,"E120.bottom"),sQuery(id+"F2.wireOp",EDGE,"E120.top"),sQuery(id+"F2.wireOp",EDGE,"E120.left"),sQuery(id+"F2.wireOp",EDGE,"E120.right")])],"isStart":true})});
            var Q1;
            Q1=makeQuery(id+"F3.boolean.opBoolean","SPLIT",FACE,{"disambiguationData":[TD([makeQuery(id+"F1.opExtrude","SWEPT_FACE",FACE,{"disambiguationData":[OSD([sQuery(id+"F0.wireOp",EDGE,"E67.MirrorCS")])]})])],"derivedFrom":makeQuery(id+"F3.opExtrude","CAP_FACE",FACE,{"disambiguationData":[OSD([sQuery(id+"F2.wireOp",EDGE,"E120.bottom"),sQuery(id+"F2.wireOp",EDGE,"E120.top"),sQuery(id+"F2.wireOp",EDGE,"E120.left"),sQuery(id+"F2.wireOp",EDGE,"E120.right")])],"isStart":true})});
            fillet(context, id + "F7", {"entities" : qUnion([Q0, Q1]), "radius" : 3 * mm, "tangentPropagation" : true, "allowEdgeOverflow" : false});
        }
        {
            var Q0;
            Q0=makeQuery(id+"F6.boolean.opBoolean","INTERSECT",EDGE,{"derivedFrom":[makeQuery(id+"F1.opExtrude","SWEPT_FACE",FACE,{"disambiguationData":[OSD([sQuery(id+"F0.wireOp",EDGE,"E114.MirrorCS")])]}),makeQuery(id+"F6.opExtrude","SWEPT_FACE",FACE,{"disambiguationData":[OSD([sQuery(id+"F5.wireOp",EDGE,"E121.top")])]})]});
            var Q1;
            Q1=makeQuery(id+"F6.boolean.opBoolean","INTERSECT",EDGE,{"derivedFrom":[makeQuery(id+"F1.opExtrude","SWEPT_FACE",FACE,{"disambiguationData":[OSD([sQuery(id+"F0.wireOp",EDGE,"E107.MirrorCS")])]}),makeQuery(id+"F6.opExtrude","SWEPT_FACE",FACE,{"disambiguationData":[OSD([sQuery(id+"F5.wireOp",EDGE,"E121.top")])]})]});
            fillet(context, id + "F8", {"entities" : qUnion([Q0, Q1]), "radius" : 5 * mm, "tangentPropagation" : true, "allowEdgeOverflow" : false});
        }
        {
            var Q0;
            {var subQ0=sQuery(id+"F5.wireOp",EDGE,"E121.top");Q0=makeQuery(id+"F6.boolean.opBoolean","SPLIT",EDGE,{"disambiguationData":[TD([makeQuery(id+"F1.opExtrude","SWEPT_FACE",FACE,{"disambiguationData":[OSD([sQuery(id+"F0.wireOp",EDGE,"E107.MirrorCS")])]})])],"derivedFrom":makeQuery(id+"F6.opExtrude","CAP_EDGE",EDGE,{"disambiguationData":[OSD([subQ0])],"isStart":true})});}
            var Q1;
            Q1=makeQuery(id+"F1.opExtrude","CAP_EDGE",EDGE,{"disambiguationData":[OSD([sQuery(id+"F0.wireOp",EDGE,"E107.MirrorCS")])],"isStart":true});
            var Q2;
            Q2=makeQuery(id+"F1.opExtrude","CAP_EDGE",EDGE,{"disambiguationData":[OSD([sQuery(id+"F0.wireOp",EDGE,"E97.MirrorCS")])],"isStart":true});
            var Q3;
            Q3=makeQuery(id+"F1.opExtrude","CAP_EDGE",EDGE,{"disambiguationData":[OSD([sQuery(id+"F0.wireOp",EDGE,"E113.MirrorCS")])],"isStart":true});
            var Q4;
            Q4=makeQuery(id+"F1.opExtrude","CAP_EDGE",EDGE,{"disambiguationData":[OSD([sQuery(id+"F0.wireOp",EDGE,"E1"),sQuery(id+"F0.wireOp",EDGE,"E81.MirrorCS")])],"isStart":true});
            var Q5;
            Q5=makeQuery(id+"F1.opExtrude","CAP_EDGE",EDGE,{"disambiguationData":[OSD([sQuery(id+"F0.wireOp",EDGE,"E51.0")])],"isStart":true});
            var Q6;
            {var subQ0=sQuery(id+"F2.wireOp",EDGE,"E120.top");var subQ1=makeQuery(id+"F1.opExtrude","SWEPT_FACE",FACE,{"disambiguationData":[OSD([sQuery(id+"F0.wireOp",EDGE,"E107.MirrorCS")])]});var subQ2=sQuery(id+"F2.wireOp",EDGE,"E120.bottom");var subQ3=sQuery(id+"F2.wireOp",EDGE,"E120.left");var subQ4=sQuery(id+"F2.wireOp",EDGE,"E120.right");Q6=makeQuery(id+"F8.opFillet","BLEND_EDGE",EDGE,{"blendedFrom":[makeQuery(id+"F6.boolean.opBoolean","INTERSECT",EDGE,{"derivedFrom":[subQ1,makeQuery(id+"F6.opExtrude","SWEPT_FACE",FACE,{"disambiguationData":[OSD([sQuery(id+"F5.wireOp",EDGE,"E121.top")])]})]}),makeQuery(id+"F3.boolean.opBoolean","SPLIT",FACE,{"disambiguationData":[TD([makeQuery(id+"F1.opExtrude","SWEPT_FACE",FACE,{"disambiguationData":[OSD([sQuery(id+"F0.wireOp",EDGE,"E2.0.1.0")])]})])],"derivedFrom":makeQuery(id+"F3.opExtrude","CAP_FACE",FACE,{"disambiguationData":[OSD([subQ2,subQ0,subQ3,subQ4])],"isStart":true})})],"blendedInto":[makeQuery(id+"F3.boolean.opBoolean","SPLIT",FACE,{"disambiguationData":[TD([makeQuery(id+"F1.opExtrude","SWEPT_FACE",FACE,{"disambiguationData":[OSD([sQuery(id+"F0.wireOp",EDGE,"E2.0.1.0")])]})])],"derivedFrom":makeQuery(id+"F3.opExtrude","CAP_FACE",FACE,{"disambiguationData":[OSD([subQ2,subQ0,subQ3,subQ4])],"isStart":true})})]});}
            var Q7;
            Q7=makeQuery(id+"F1.opExtrude","CAP_EDGE",EDGE,{"disambiguationData":[OSD([sQuery(id+"F0.wireOp",EDGE,"E2.0.1.0")])],"isStart":true});
            var Q8;
            Q8=makeQuery(id+"F1.opExtrude","CAP_EDGE",EDGE,{"disambiguationData":[OSD([sQuery(id+"F0.wireOp",EDGE,"E25.0")])],"isStart":true});
            var Q9;
            Q9=makeQuery(id+"F1.opExtrude","CAP_EDGE",EDGE,{"disambiguationData":[OSD([sQuery(id+"F0.wireOp",EDGE,"E2.0.2.0")])],"isStart":true});
            var Q10;
            Q10=makeQuery(id+"F1.opExtrude","CAP_EDGE",EDGE,{"disambiguationData":[OSD([sQuery(id+"F0.wireOp",EDGE,"E12.0")])],"isStart":true});
            var Q11;
            Q11=makeQuery(id+"F1.opExtrude","CAP_EDGE",EDGE,{"disambiguationData":[OSD([sQuery(id+"F0.wireOp",EDGE,"E2.1.2.0")])],"isStart":true});
            var Q12;
            Q12=makeQuery(id+"F1.opExtrude","CAP_EDGE",EDGE,{"disambiguationData":[OSD([sQuery(id+"F0.wireOp",EDGE,"E11.0")])],"isStart":true});
            var Q13;
            Q13=makeQuery(id+"F1.opExtrude","CAP_EDGE",EDGE,{"disambiguationData":[OSD([sQuery(id+"F0.wireOp",EDGE,"E2.1.1.0")])],"isStart":true});
            var Q14;
            Q14=makeQuery(id+"F1.opExtrude","CAP_EDGE",EDGE,{"disambiguationData":[OSD([sQuery(id+"F0.wireOp",EDGE,"E50.0")])],"isStart":true});
            var Q15;
            Q15=makeQuery(id+"F1.opExtrude","CAP_EDGE",EDGE,{"disambiguationData":[OSD([sQuery(id+"F0.wireOp",EDGE,"E119.MirrorCS")])],"isStart":true});
            var Q16;
            Q16=makeQuery(id+"F1.opExtrude","CAP_EDGE",EDGE,{"disambiguationData":[OSD([sQuery(id+"F0.wireOp",EDGE,"E2.1.0.0"),sQuery(id+"F0.wireOp",EDGE,"E59.MirrorCS")])],"isStart":true});
            var Q17;
            Q17=makeQuery(id+"F1.opExtrude","CAP_EDGE",EDGE,{"disambiguationData":[OSD([sQuery(id+"F0.wireOp",EDGE,"E91.MirrorCS")])],"isStart":true});
            var Q18;
            Q18=makeQuery(id+"F1.opExtrude","CAP_EDGE",EDGE,{"disambiguationData":[OSD([sQuery(id+"F0.wireOp",EDGE,"E114.MirrorCS")])],"isStart":true});
            var Q19;
            {var subQ0=sQuery(id+"F2.wireOp",EDGE,"E120.top");var subQ1=makeQuery(id+"F1.opExtrude","SWEPT_FACE",FACE,{"disambiguationData":[OSD([sQuery(id+"F0.wireOp",EDGE,"E114.MirrorCS")])]});var subQ2=sQuery(id+"F2.wireOp",EDGE,"E120.bottom");var subQ3=sQuery(id+"F2.wireOp",EDGE,"E120.left");var subQ4=sQuery(id+"F2.wireOp",EDGE,"E120.right");Q19=makeQuery(id+"F8.opFillet","BLEND_EDGE",EDGE,{"blendedFrom":[makeQuery(id+"F6.boolean.opBoolean","INTERSECT",EDGE,{"derivedFrom":[subQ1,makeQuery(id+"F6.opExtrude","SWEPT_FACE",FACE,{"disambiguationData":[OSD([sQuery(id+"F5.wireOp",EDGE,"E121.top")])]})]}),makeQuery(id+"F3.boolean.opBoolean","SPLIT",FACE,{"disambiguationData":[TD([makeQuery(id+"F1.opExtrude","SWEPT_FACE",FACE,{"disambiguationData":[OSD([sQuery(id+"F0.wireOp",EDGE,"E2.0.1.0")])]})])],"derivedFrom":makeQuery(id+"F3.opExtrude","CAP_FACE",FACE,{"disambiguationData":[OSD([subQ2,subQ0,subQ3,subQ4])],"isStart":true})})],"blendedInto":[makeQuery(id+"F3.boolean.opBoolean","SPLIT",FACE,{"disambiguationData":[TD([makeQuery(id+"F1.opExtrude","SWEPT_FACE",FACE,{"disambiguationData":[OSD([sQuery(id+"F0.wireOp",EDGE,"E2.0.1.0")])]})])],"derivedFrom":makeQuery(id+"F3.opExtrude","CAP_FACE",FACE,{"disambiguationData":[OSD([subQ2,subQ0,subQ3,subQ4])],"isStart":true})})]});}
            var Q20;
            {var subQ0=sQuery(id+"F5.wireOp",EDGE,"E121.top");Q20=makeQuery(id+"F6.boolean.opBoolean","SPLIT",EDGE,{"disambiguationData":[TD([makeQuery(id+"F1.opExtrude","SWEPT_FACE",FACE,{"disambiguationData":[OSD([sQuery(id+"F0.wireOp",EDGE,"E114.MirrorCS")])]})])],"derivedFrom":makeQuery(id+"F6.opExtrude","CAP_EDGE",EDGE,{"disambiguationData":[OSD([subQ0])],"isStart":true})});}
            fillet(context, id + "F9", {"entities" : qUnion([Q0, Q1, Q2, Q3, Q4, Q5, Q6, Q7, Q8, Q9, Q10, Q11, Q12, Q13, Q14, Q15, Q16, Q17, Q18, Q19, Q20]), "radius" : 3 * mm, "tangentPropagation" : true, "allowEdgeOverflow" : false});
        }
        {
            var Q0;
            Q0=qCreatedBy(makeId("Top.planeOp"),FACE);
            var sketch = newSketch(context, id + "F10", { "sketchPlane" : qUnion([Q0])});
            skLineSegment(sketch, "E122.bottom", {"start": v(-75.4, 0) * mm, "end": v(66.9, 0) * mm});
            skLineSegment(sketch, "E122.top", {"start": v(-75.4, 148.67) * mm, "end": v(66.9, 148.67) * mm});
            skLineSegment(sketch, "E122.left", {"start": v(-75.4, 0) * mm, "end": v(-75.4, 148.67) * mm});
            skLineSegment(sketch, "E122.right", {"start": v(66.9, 0) * mm, "end": v(66.9, 148.67) * mm});
            skSolve(sketch);
        }
        {
            var Q0;
            Q0 = qSketchRegion(id + "F10", true);
            extrude(context, id + "F11", {"entities" : qUnion([Q0]), "operationType" : NewBodyOperationType.REMOVE, "depth" : 10 * mm, "offsetDistance" : 25 * mm, "hasSecondDirection" : true, "secondDirectionOppositeDirection" : true, "secondDirectionDepth" : 10 * mm});
        }
        {
            var Q0;
            Q0=qCreatedBy(makeId("Top.planeOp"),FACE);
            var sketch = newSketch(context, id + "F12", { "sketchPlane" : qUnion([Q0])});
            skLineSegment(sketch, "E123.bottom", {"start": v(-64.95, 0) * mm, "end": v(63.48, 0) * mm});
            skLineSegment(sketch, "E123.top", {"start": v(-64.95, -146.15) * mm, "end": v(63.48, -146.15) * mm});
            skLineSegment(sketch, "E123.left", {"start": v(-64.95, 0) * mm, "end": v(-64.95, -146.15) * mm});
            skLineSegment(sketch, "E123.right", {"start": v(63.48, 0) * mm, "end": v(63.48, -146.15) * mm});
            skSolve(sketch);
        }
        {
            var Q0;
            Q0 = qSketchRegion(id + "F12", true);
            extrude(context, id + "F13", {"entities" : qUnion([Q0]), "operationType" : NewBodyOperationType.REMOVE, "oppositeDirection" : true, "depth" : 2 * mm, "offsetDistance" : 25 * mm});
        }
    });
